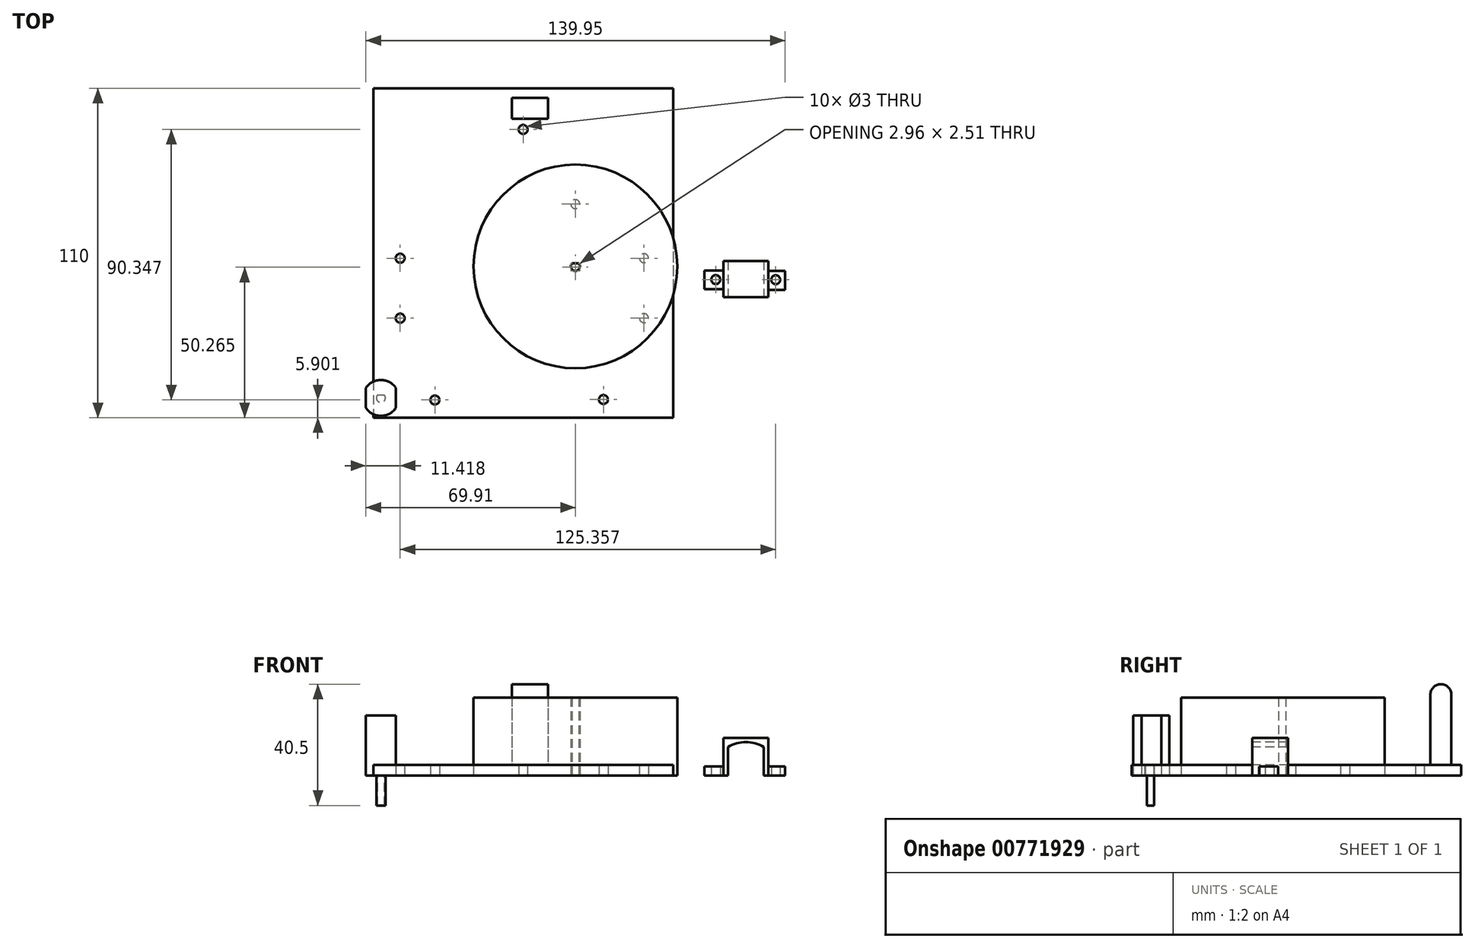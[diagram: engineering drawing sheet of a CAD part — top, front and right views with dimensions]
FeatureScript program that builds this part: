
annotation { "Feature Type Name" : "Feature", "Feature Type Description" : "" }
export const myFeature = defineFeature(function(context is Context, id is Id, definition is map)
    precondition{}
    {
        {
            var Q0;
            Q0=qCreatedBy(makeId("Top.planeOp"),FACE);
            var sketch = newSketch(context, id + "F0", { "sketchPlane" : qUnion([Q0])});
            skCircle(sketch, "E0", {"center": v(0, 0) * mm, "radius": 34 * mm});
            skCircle(sketch, "E1", {"center": v(0, 0) * mm, "radius": 1.5 * mm});
            skLineSegment(sketch, "E2", {"start": v(-1.1, 1.01) * mm, "end": v(1.1, 1.01) * mm});
            skSolve(sketch);
        }
        {
            var Q0;
            Q0 = qSketchRegion(id + "F0", true);
            extrude(context, id + "F1", {"entities" : qUnion([Q0]), "depth" : 26 * mm, "offsetDistance" : 25 * mm});
        }
        {
            var Q0;
            {var subQ0=sQuery(id+"F0.wireOp",EDGE,"E2");Q0=makeQuery(id+"F0.imprint","IMPRINT",FACE,{"disambiguationData":[TD([[makeQuery(id+"F0.imprint","IMPRINT",EDGE,{"derivedFrom":subQ0}),1.0]])]});}
            extrude(context, id + "F2", {"entities" : qUnion([Q0]), "operationType" : NewBodyOperationType.ADD, "depth" : 26 * mm, "offsetDistance" : 25 * mm});
        }
        {
            var Q0;
            Q0=qCreatedBy(makeId("Top.planeOp"),FACE);
            var sketch = newSketch(context, id + "F3", { "sketchPlane" : qUnion([Q0])});
            skLineSegment(sketch, "E3", {"start": v(-69.91, -47.41) * mm, "end": v(-69.91, -40.41) * mm});
            skLineSegment(sketch, "E4", {"start": v(-69.91, -47.41) * mm, "end": v(-59.91, -47.41) * mm});
            skLineSegment(sketch, "E5", {"start": v(-69.91, -40.41) * mm, "end": v(-59.91, -40.41) * mm});
            skLineSegment(sketch, "E6", {"start": v(-59.91, -40.41) * mm, "end": v(-59.91, -47.41) * mm});
            skPoint(sketch, "E7", {"position": v(-64.91, -43.91) * mm});
            skPoint(sketch, "E7.positionSnap0", {"position": v(-69.91, -43.91) * mm});
            skPoint(sketch, "E7.positionSnap1", {"position": v(-64.91, -47.41) * mm});
            skCircle(sketch, "E8", {"center": v(-64.91, -43.91) * mm, "radius": 6 * mm});
            skCircle(sketch, "E9", {"center": v(-64.91, -43.91) * mm, "radius": 1.5 * mm});
            skLineSegment(sketch, "E10", {"start": v(-66.03, -42.91) * mm, "end": v(-63.8, -42.91) * mm});
            skSolve(sketch);
        }
        {
            var Q0;
            {var subQ0=sQuery(id+"F3.wireOp",EDGE,"E8");var subQ10=sQuery(id+"F3.wireOp",EDGE,"E3");var subQ11=makeQuery(id+"F3.imprint","INTERSECT",VERTEX,{"disambiguationData":[OD(0.0)],"derivedFrom":[subQ10,subQ0]});Q0=makeQuery(id+"F3.imprint","IMPRINT",FACE,{"disambiguationData":[TD([[makeQuery(id+"F3.imprint","IMPRINT",EDGE,{"disambiguationData":[TD([[subQ11,-1.0]])],"derivedFrom":subQ10}),-1.0]])]});}
            extrude(context, id + "F4", {"entities" : qUnion([Q0]), "depth" : 20 * mm, "offsetDistance" : 25 * mm});
        }
        {
            var Q0;
            {var subQ0=sQuery(id+"F3.wireOp",EDGE,"E8");var subQ1=sQuery(id+"F3.wireOp",EDGE,"E4");var subQ2=makeQuery(id+"F3.imprint","INTERSECT",VERTEX,{"disambiguationData":[OD(0.0)],"derivedFrom":[subQ1,subQ0]});Q0=makeQuery(id+"F3.imprint","IMPRINT",FACE,{"disambiguationData":[TD([[makeQuery(id+"F3.imprint","IMPRINT",EDGE,{"disambiguationData":[TD([[subQ2,-1.0]])],"derivedFrom":subQ1}),-1.0]])]});}
            var Q1;
            {var subQ0=sQuery(id+"F3.wireOp",EDGE,"E10");Q1=makeQuery(id+"F3.imprint","IMPRINT",FACE,{"disambiguationData":[TD([[makeQuery(id+"F3.imprint","IMPRINT",EDGE,{"derivedFrom":subQ0}),1.0]])]});}
            var Q2;
            {var subQ0=sQuery(id+"F3.wireOp",EDGE,"E10");Q2=makeQuery(id+"F3.imprint","IMPRINT",FACE,{"disambiguationData":[TD([[makeQuery(id+"F3.imprint","IMPRINT",EDGE,{"derivedFrom":subQ0}),-1.0]])]});}
            extrude(context, id + "F5", {"entities" : qUnion([Q0, Q1, Q2]), "operationType" : NewBodyOperationType.ADD, "depth" : 20 * mm, "offsetDistance" : 25 * mm});
        }
        {
            var Q0;
            {var subQ0=sQuery(id+"F3.wireOp",EDGE,"E8");var subQ1=sQuery(id+"F3.wireOp",EDGE,"E5");var subQ2=makeQuery(id+"F3.imprint","INTERSECT",VERTEX,{"disambiguationData":[OD(0.0)],"derivedFrom":[subQ1,subQ0]});Q0=makeQuery(id+"F3.imprint","IMPRINT",FACE,{"disambiguationData":[TD([[makeQuery(id+"F3.imprint","IMPRINT",EDGE,{"disambiguationData":[TD([[subQ2,-1.0]])],"derivedFrom":subQ1}),1.0]])]});}
            extrude(context, id + "F6", {"entities" : qUnion([Q0]), "operationType" : NewBodyOperationType.ADD, "depth" : 20 * mm, "offsetDistance" : 25 * mm});
        }
        {
            var Q0;
            {var subQ0=sQuery(id+"F3.wireOp",EDGE,"E10");Q0=makeQuery(id+"F3.imprint","IMPRINT",FACE,{"disambiguationData":[TD([[makeQuery(id+"F3.imprint","IMPRINT",EDGE,{"derivedFrom":subQ0}),-1.0]])]});}
            extrude(context, id + "F7", {"entities" : qUnion([Q0]), "oppositeDirection" : true, "depth" : 10 * mm, "offsetDistance" : 25 * mm});
        }
        {
            var Q0;
            Q0=qCreatedBy(makeId("Top.planeOp"),FACE);
            var sketch = newSketch(context, id + "F8", { "sketchPlane" : qUnion([Q0])});
            skLineSegment(sketch, "E11.bottom", {"start": v(-67.37, 59.5) * mm, "end": v(32.63, 59.5) * mm});
            skLineSegment(sketch, "E11.top", {"start": v(-67.37, -50.5) * mm, "end": v(32.63, -50.5) * mm});
            skLineSegment(sketch, "E11.left", {"start": v(-67.37, 59.5) * mm, "end": v(-67.37, -50.5) * mm});
            skLineSegment(sketch, "E11.right", {"start": v(32.63, 59.5) * mm, "end": v(32.63, -50.5) * mm});
            skCircle(sketch, "E12", {"center": v(-46.88, -44.6) * mm, "radius": 1.5 * mm});
            skCircle(sketch, "E13", {"center": v(9.38, -44.45) * mm, "radius": 1.5 * mm});
            skCircle(sketch, "E14", {"center": v(-58.5, -17.28) * mm, "radius": 1.5 * mm});
            skLineSegment(sketch, "E15", {"start": v(-58.5, -17.28) * mm, "end": v(-58.5, 2.72) * mm});
            skCircle(sketch, "E16", {"center": v(-58.5, 2.72) * mm, "radius": 1.5 * mm});
            skLineSegment(sketch, "E17", {"start": v(22.9, 2.72) * mm, "end": v(22.9, -17.28) * mm});
            skCircle(sketch, "E18", {"center": v(22.9, 2.72) * mm, "radius": 1.5 * mm});
            skCircle(sketch, "E19", {"center": v(22.9, -17.28) * mm, "radius": 1.5 * mm});
            skCircle(sketch, "E20", {"center": v(-17.43, 45.74) * mm, "radius": 1.5 * mm});
            skCircle(sketch, "E21", {"center": v(0, 20.81) * mm, "radius": 1.5 * mm});
            skLineSegment(sketch, "E22.bottom", {"start": v(-21.16, 56.26) * mm, "end": v(-9.16, 56.26) * mm});
            skLineSegment(sketch, "E22.top", {"start": v(-21.16, 49.26) * mm, "end": v(-9.16, 49.26) * mm});
            skLineSegment(sketch, "E22.left", {"start": v(-21.16, 56.26) * mm, "end": v(-21.16, 49.26) * mm});
            skLineSegment(sketch, "E22.right", {"start": v(-9.16, 56.26) * mm, "end": v(-9.16, 49.26) * mm});
            skSolve(sketch);
        }
        {
            var Q0;
            Q0=makeQuery(id+"F8.imprint","IMPRINT",FACE,{"disambiguationData":[TD([[makeQuery(id+"F8.imprint","IMPRINT",EDGE,{"derivedFrom":sQuery(id+"F8.wireOp",EDGE,"E11.bottom")}),-1.0]])]});
            extrude(context, id + "F9", {"entities" : qUnion([Q0]), "depth" : 3.5 * mm, "offsetDistance" : 25 * mm});
        }
        {
            var Q0;
            Q0=makeQuery(id+"F8.imprint","IMPRINT",FACE,{"disambiguationData":[TD([[makeQuery(id+"F8.imprint","IMPRINT",EDGE,{"derivedFrom":sQuery(id+"F8.wireOp",EDGE,"E22.bottom")}),-1.0]])]});
            extrude(context, id + "F10", {"entities" : qUnion([Q0]), "operationType" : NewBodyOperationType.ADD, "depth" : 30.5 * mm, "offsetDistance" : 25 * mm});
        }
        {
            var Q0;
            Q0=makeQuery(id+"F10.opExtrude","CAP_EDGE",EDGE,{"disambiguationData":[OSD([sQuery(id+"F8.wireOp",EDGE,"E22.top")])],"isStart":false});
            fillet(context, id + "F11", {"entities" : qUnion([Q0]), "radius" : 3.5 * mm, "tangentPropagation" : true, "allowEdgeOverflow" : false});
        }
        {
            var Q0;
            Q0=makeQuery(id+"F10.opExtrude","CAP_EDGE",EDGE,{"disambiguationData":[OSD([sQuery(id+"F8.wireOp",EDGE,"E22.bottom")])],"isStart":false});
            fillet(context, id + "F12", {"entities" : qUnion([Q0]), "radius" : 3.5 * mm, "tangentPropagation" : true, "allowEdgeOverflow" : false});
        }
        {
            var Q0;
            Q0=qCreatedBy(makeId("Top.planeOp"),FACE);
            var sketch = newSketch(context, id + "F13", { "sketchPlane" : qUnion([Q0])});
            skLineSegment(sketch, "E23.bottom", {"start": v(49.4, 1.78) * mm, "end": v(64.4, 1.78) * mm});
            skLineSegment(sketch, "E23.top", {"start": v(49.4, -10.22) * mm, "end": v(64.4, -10.22) * mm});
            skLineSegment(sketch, "E23.left", {"start": v(49.4, 1.78) * mm, "end": v(49.4, -10.22) * mm});
            skLineSegment(sketch, "E23.right", {"start": v(64.4, 1.78) * mm, "end": v(64.4, -10.22) * mm});
            skLineSegment(sketch, "E24.bottom", {"start": v(49.4, -1.4) * mm, "end": v(43.1, -1.4) * mm});
            skLineSegment(sketch, "E24.top", {"start": v(49.4, -7.65) * mm, "end": v(43.1, -7.65) * mm});
            skLineSegment(sketch, "E24.left", {"start": v(49.4, -1.4) * mm, "end": v(49.4, -7.65) * mm});
            skLineSegment(sketch, "E24.right", {"start": v(43.1, -1.4) * mm, "end": v(43.1, -7.65) * mm});
            skLineSegment(sketch, "E25.bottom", {"start": v(64.4, -1.5) * mm, "end": v(70.04, -1.5) * mm});
            skLineSegment(sketch, "E25.top", {"start": v(64.4, -7.89) * mm, "end": v(70.04, -7.89) * mm});
            skLineSegment(sketch, "E25.left", {"start": v(64.4, -1.5) * mm, "end": v(64.4, -7.89) * mm});
            skLineSegment(sketch, "E25.right", {"start": v(70.04, -1.5) * mm, "end": v(70.04, -7.89) * mm});
            skCircle(sketch, "E26", {"center": v(46.87, -4.4) * mm, "radius": 1.5 * mm});
            skCircle(sketch, "E27", {"center": v(66.87, -4.44) * mm, "radius": 1.5 * mm});
            skSolve(sketch);
        }
        {
            var Q0;
            {var subQ1=sQuery(id+"F13.wireOp",EDGE,"E23.bottom");Q0=makeQuery(id+"F13.imprint","IMPRINT",FACE,{"disambiguationData":[TD([[makeQuery(id+"F13.imprint","IMPRINT",EDGE,{"derivedFrom":subQ1}),-1.0]])]});}
            extrude(context, id + "F14", {"entities" : qUnion([Q0]), "depth" : 12.5 * mm, "offsetDistance" : 25 * mm});
        }
        {
            var Q0;
            {var subQ1=sQuery(id+"F13.wireOp",EDGE,"E24.bottom");Q0=makeQuery(id+"F13.imprint","IMPRINT",FACE,{"disambiguationData":[TD([[makeQuery(id+"F13.imprint","IMPRINT",EDGE,{"derivedFrom":subQ1}),1.0]])]});}
            extrude(context, id + "F15", {"entities" : qUnion([Q0]), "operationType" : NewBodyOperationType.ADD, "depth" : 3 * mm, "offsetDistance" : 25 * mm});
        }
        {
            var Q0;
            {var subQ1=sQuery(id+"F13.wireOp",EDGE,"E25.bottom");Q0=makeQuery(id+"F13.imprint","IMPRINT",FACE,{"disambiguationData":[TD([[makeQuery(id+"F13.imprint","IMPRINT",EDGE,{"derivedFrom":subQ1}),-1.0]])]});}
            extrude(context, id + "F16", {"entities" : qUnion([Q0]), "operationType" : NewBodyOperationType.ADD, "depth" : 3 * mm, "offsetDistance" : 25 * mm});
        }
        {
            var Q0;
            Q0=makeQuery(id+"F14.opExtrude","SWEPT_FACE",FACE,{"disambiguationData":[OSD([sQuery(id+"F13.wireOp",EDGE,"E23.top")])]});
            var sketch = newSketch(context, id + "F17", { "sketchPlane" : qUnion([Q0])});
            skLineSegment(sketch, "E28.bottom", {"start": v(50.9, 9.5) * mm, "end": v(62.9, 9.5) * mm});
            skLineSegment(sketch, "E28.top", {"start": v(50.9, -0.5) * mm, "end": v(62.9, -0.5) * mm});
            skLineSegment(sketch, "E28.left", {"start": v(50.9, 9.5) * mm, "end": v(50.9, -0.5) * mm});
            skLineSegment(sketch, "E28.right", {"start": v(62.9, 9.5) * mm, "end": v(62.9, -0.5) * mm});
            skArc(sketch, "E29", {"start": v(62.9, 9.5) * mm, "mid": v(56.9, 11.14) * mm, "end": v(50.9, 9.5) * mm});
            skSolve(sketch);
        }
        {
            var Q0;
            Q0 = qSketchRegion(id + "F17", true);
            extrude(context, id + "F18", {"entities" : qUnion([Q0]), "operationType" : NewBodyOperationType.REMOVE, "oppositeDirection" : true, "depth" : 25 * mm, "offsetDistance" : 25 * mm});
        }
    });
